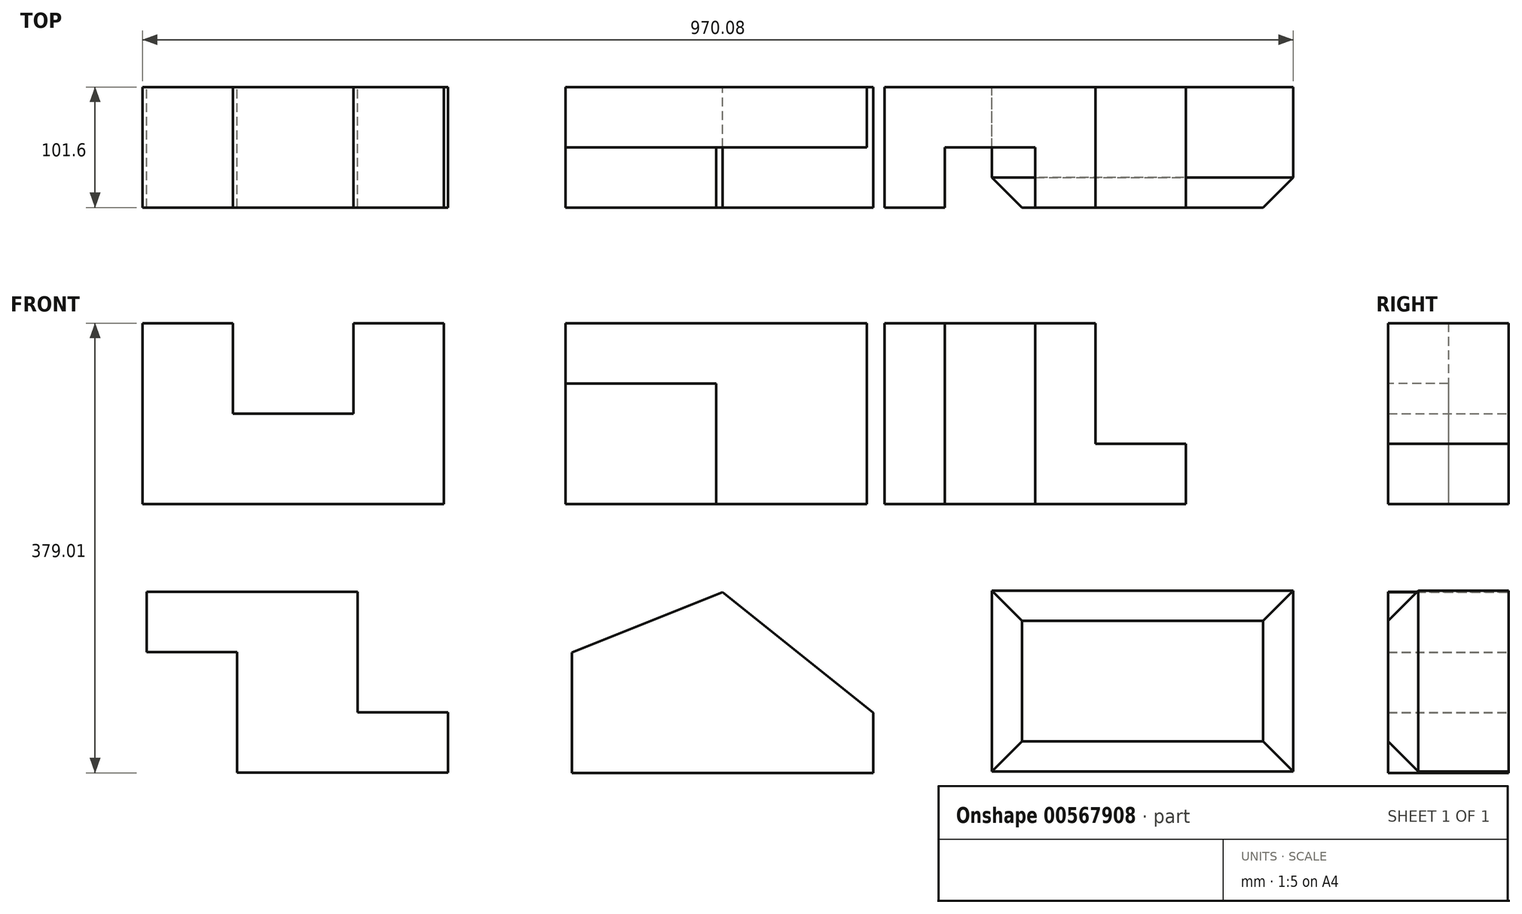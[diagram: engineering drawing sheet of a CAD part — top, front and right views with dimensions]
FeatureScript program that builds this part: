
annotation { "Feature Type Name" : "Feature", "Feature Type Description" : "" }
export const myFeature = defineFeature(function(context is Context, id is Id, definition is map)
    precondition{}
    {
        {
            var Q0;
            Q0=qCreatedBy(makeId("Front.planeOp"),FACE);
            var sketch = newSketch(context, id + "F0", { "sketchPlane" : qUnion([Q0])});
            skLineSegment(sketch, "E0", {"start": v(0, 0) * mm, "end": v(127, 0) * mm});
            skLineSegment(sketch, "E1", {"start": v(0, 0) * mm, "end": v(-127, 0) * mm});
            skLineSegment(sketch, "E2", {"start": v(127, 0) * mm, "end": v(127, 152.4) * mm});
            skLineSegment(sketch, "E3", {"start": v(127, 152.4) * mm, "end": v(50.8, 152.4) * mm});
            skLineSegment(sketch, "E4", {"start": v(50.8, 152.4) * mm, "end": v(50.8, 76.2) * mm});
            skLineSegment(sketch, "E5", {"start": v(50.8, 76.2) * mm, "end": v(-50.8, 76.2) * mm});
            skLineSegment(sketch, "E6", {"start": v(-50.8, 76.2) * mm, "end": v(-50.8, 152.4) * mm});
            skLineSegment(sketch, "E7", {"start": v(-50.8, 152.4) * mm, "end": v(-127, 152.4) * mm});
            skLineSegment(sketch, "E8", {"start": v(-127, 152.4) * mm, "end": v(-127, 0) * mm});
            skSolve(sketch);
        }
        {
            var Q0;
            Q0 = qSketchRegion(id + "F0", true);
            extrude(context, id + "F1", {"entities" : qUnion([Q0]), "depth" : 101.6 * mm, "offsetDistance" : 25.4 * mm});
        }
        {
            var Q0;
            Q0=qCreatedBy(makeId("Top.planeOp"),FACE);
            var sketch = newSketch(context, id + "F2", { "sketchPlane" : qUnion([Q0])});
            skLineSegment(sketch, "E9", {"start": v(229.7, 0) * mm, "end": v(229.7, -101.6) * mm});
            skLineSegment(sketch, "E10", {"start": v(229.7, -101.6) * mm, "end": v(356.7, -101.6) * mm});
            skLineSegment(sketch, "E11", {"start": v(356.7, -101.6) * mm, "end": v(356.7, -50.8) * mm});
            skLineSegment(sketch, "E12", {"start": v(356.7, -50.8) * mm, "end": v(483.7, -50.8) * mm});
            skLineSegment(sketch, "E13", {"start": v(229.7, -101.6) * mm, "end": v(220.96, -101.6) * mm});
            skLineSegment(sketch, "E14", {"start": v(483.7, -50.8) * mm, "end": v(483.7, 0) * mm});
            skLineSegment(sketch, "E15", {"start": v(483.7, 0) * mm, "end": v(229.7, 0) * mm});
            skSolve(sketch);
        }
        {
            var Q0;
            Q0 = qSketchRegion(id + "F2", true);
            extrude(context, id + "F3", {"entities" : qUnion([Q0]), "depth" : 152.4 * mm, "offsetDistance" : 25.4 * mm});
        }
        {
            var Q0;
            Q0=makeQuery(id+"F3.opExtrude","SWEPT_FACE",FACE,{"disambiguationData":[OSD([sQuery(id+"F2.wireOp",EDGE,"E10")])]});
            var sketch = newSketch(context, id + "F4", { "sketchPlane" : qUnion([Q0])});
            skLineSegment(sketch, "E16.bottom", {"start": v(229.7, 152.4) * mm, "end": v(356.7, 152.4) * mm});
            skLineSegment(sketch, "E16.top", {"start": v(229.7, 101.6) * mm, "end": v(356.7, 101.6) * mm});
            skLineSegment(sketch, "E16.left", {"start": v(229.7, 152.4) * mm, "end": v(229.7, 101.6) * mm});
            skLineSegment(sketch, "E16.right", {"start": v(356.7, 152.4) * mm, "end": v(356.7, 101.6) * mm});
            skSolve(sketch);
        }
        {
            var Q0;
            Q0=makeQuery(id+"F4.imprint","IMPRINT",FACE,{"disambiguationData":[TD([[makeQuery(id+"F4.imprint","IMPRINT",EDGE,{"derivedFrom":sQuery(id+"F4.wireOp",EDGE,"E16.bottom")}),-1.0]])]});
            extrude(context, id + "F5", {"entities" : qUnion([Q0]), "operationType" : NewBodyOperationType.REMOVE, "oppositeDirection" : true, "depth" : 50.8 * mm, "offsetDistance" : 25.4 * mm});
        }
        {
            var Q0;
            Q0=qCreatedBy(makeId("Top.planeOp"),FACE);
            var sketch = newSketch(context, id + "F6", { "sketchPlane" : qUnion([Q0])});
            skLineSegment(sketch, "E17", {"start": v(498.64, -101.6) * mm, "end": v(498.64, 0) * mm});
            skLineSegment(sketch, "E18", {"start": v(498.64, -101.6) * mm, "end": v(549.44, -101.6) * mm});
            skLineSegment(sketch, "E19", {"start": v(549.44, -101.6) * mm, "end": v(549.44, -50.8) * mm});
            skLineSegment(sketch, "E20", {"start": v(549.44, -50.8) * mm, "end": v(625.64, -50.8) * mm});
            skLineSegment(sketch, "E21", {"start": v(625.64, -50.8) * mm, "end": v(625.64, -101.6) * mm});
            skLineSegment(sketch, "E22", {"start": v(625.64, -101.6) * mm, "end": v(752.64, -101.6) * mm});
            skLineSegment(sketch, "E23", {"start": v(752.64, -101.6) * mm, "end": v(752.64, 0) * mm});
            skLineSegment(sketch, "E24", {"start": v(752.64, 0) * mm, "end": v(498.64, 0) * mm});
            skSolve(sketch);
        }
        {
            var Q0;
            Q0 = qSketchRegion(id + "F6", true);
            extrude(context, id + "F7", {"entities" : qUnion([Q0]), "depth" : 152.4 * mm, "offsetDistance" : 25.4 * mm});
        }
        {
            var Q0;
            Q0=makeQuery(id+"F7.opExtrude","CAP_FACE",FACE,{"disambiguationData":[OSD([sQuery(id+"F6.wireOp",EDGE,"E17"),sQuery(id+"F6.wireOp",EDGE,"E18"),sQuery(id+"F6.wireOp",EDGE,"E19"),sQuery(id+"F6.wireOp",EDGE,"E20"),sQuery(id+"F6.wireOp",EDGE,"E21"),sQuery(id+"F6.wireOp",EDGE,"E22"),sQuery(id+"F6.wireOp",EDGE,"E23"),sQuery(id+"F6.wireOp",EDGE,"E24")])],"isStart":false});
            var sketch = newSketch(context, id + "F8", { "sketchPlane" : qUnion([Q0])});
            skLineSegment(sketch, "E25.bottom", {"start": v(752.64, -101.6) * mm, "end": v(676.44, -101.6) * mm});
            skLineSegment(sketch, "E25.top", {"start": v(752.64, 0) * mm, "end": v(676.44, 0) * mm});
            skLineSegment(sketch, "E25.left", {"start": v(752.64, -101.6) * mm, "end": v(752.64, 0) * mm});
            skLineSegment(sketch, "E25.right", {"start": v(676.44, -101.6) * mm, "end": v(676.44, 0) * mm});
            skSolve(sketch);
        }
        {
            var Q0;
            Q0=makeQuery(id+"F8.imprint","IMPRINT",FACE,{"disambiguationData":[TD([[makeQuery(id+"F8.imprint","IMPRINT",EDGE,{"derivedFrom":sQuery(id+"F8.wireOp",EDGE,"E25.bottom")}),1.0]])]});
            extrude(context, id + "F9", {"entities" : qUnion([Q0]), "operationType" : NewBodyOperationType.REMOVE, "oppositeDirection" : true, "depth" : 101.6 * mm, "offsetDistance" : 25.4 * mm});
        }
        {
            var Q0;
            Q0=qCreatedBy(makeId("Front.planeOp"),FACE);
            var sketch = newSketch(context, id + "F10", { "sketchPlane" : qUnion([Q0])});
            skLineSegment(sketch, "E26", {"start": v(-123.4, 0) * mm, "end": v(-123.4, -74.16) * mm});
            skLineSegment(sketch, "E27", {"start": v(-123.4, -74.16) * mm, "end": v(-123.4, -124.96) * mm});
            skLineSegment(sketch, "E28", {"start": v(-123.4, -74.16) * mm, "end": v(54.4, -74.16) * mm});
            skLineSegment(sketch, "E29", {"start": v(54.4, -74.16) * mm, "end": v(54.4, -175.76) * mm});
            skLineSegment(sketch, "E30", {"start": v(54.4, -175.76) * mm, "end": v(130.6, -175.76) * mm});
            skLineSegment(sketch, "E31", {"start": v(130.6, -175.76) * mm, "end": v(130.6, -226.56) * mm});
            skLineSegment(sketch, "E32", {"start": v(130.6, -226.56) * mm, "end": v(-47.2, -226.56) * mm});
            skLineSegment(sketch, "E33", {"start": v(-47.2, -226.56) * mm, "end": v(-47.2, -124.96) * mm});
            skLineSegment(sketch, "E34", {"start": v(-47.2, -124.96) * mm, "end": v(-123.4, -124.96) * mm});
            skSolve(sketch);
        }
        {
            var Q0;
            Q0 = qSketchRegion(id + "F10", true);
            extrude(context, id + "F11", {"entities" : qUnion([Q0]), "depth" : 101.6 * mm, "offsetDistance" : 25.4 * mm});
        }
        {
            var Q0;
            Q0=qCreatedBy(makeId("Front.planeOp"),FACE);
            var sketch = newSketch(context, id + "F12", { "sketchPlane" : qUnion([Q0])});
            skLineSegment(sketch, "E35", {"start": v(234.94, -226.61) * mm, "end": v(488.94, -226.61) * mm});
            skLineSegment(sketch, "E36", {"start": v(488.94, -226.61) * mm, "end": v(488.94, -175.81) * mm});
            skLineSegment(sketch, "E37", {"start": v(234.94, -226.61) * mm, "end": v(234.94, -125.01) * mm});
            skLineSegment(sketch, "E38", {"start": v(234.94, -226.61) * mm, "end": v(361.94, -226.61) * mm});
            skLineSegment(sketch, "E39", {"start": v(361.94, -74.21) * mm, "end": v(234.94, -125.01) * mm});
            skLineSegment(sketch, "E40", {"start": v(361.94, -74.21) * mm, "end": v(488.94, -175.81) * mm});
            skSolve(sketch);
        }
        {
            var Q0;
            Q0 = qSketchRegion(id + "F12", true);
            extrude(context, id + "F13", {"entities" : qUnion([Q0]), "depth" : 101.6 * mm, "offsetDistance" : 25.4 * mm});
        }
        {
            var Q0;
            Q0=qCreatedBy(makeId("Front.planeOp"),FACE);
            var sketch = newSketch(context, id + "F14", { "sketchPlane" : qUnion([Q0])});
            skLineSegment(sketch, "E41", {"start": v(589.08, -225.44) * mm, "end": v(589.08, -73.04) * mm});
            skLineSegment(sketch, "E42", {"start": v(589.08, -73.04) * mm, "end": v(843.08, -73.04) * mm});
            skLineSegment(sketch, "E43", {"start": v(843.08, -73.04) * mm, "end": v(843.08, -225.44) * mm});
            skLineSegment(sketch, "E44", {"start": v(843.08, -225.44) * mm, "end": v(589.08, -225.44) * mm});
            skSolve(sketch);
        }
        {
            var Q0;
            Q0 = qSketchRegion(id + "F14", true);
            extrude(context, id + "F15", {"entities" : qUnion([Q0]), "depth" : 101.6 * mm, "offsetDistance" : 25.4 * mm});
        }
        {
            var Q0;
            Q0=makeQuery(id+"F15.opExtrude","CAP_EDGE",EDGE,{"disambiguationData":[OSD([sQuery(id+"F14.wireOp",EDGE,"E42")])],"isStart":false});
            chamfer(context, id + "F16", {"entities" : qUnion([Q0]), "width" : 25.4 * mm, "tangentPropagation" : true});
        }
        {
            var Q0;
            Q0=makeQuery(id+"F15.opExtrude","CAP_EDGE",EDGE,{"disambiguationData":[OSD([sQuery(id+"F14.wireOp",EDGE,"E43")])],"isStart":false});
            var Q1;
            Q1=makeQuery(id+"F15.opExtrude","CAP_EDGE",EDGE,{"disambiguationData":[OSD([sQuery(id+"F14.wireOp",EDGE,"E44")])],"isStart":false});
            chamfer(context, id + "F17", {"entities" : qUnion([Q0, Q1]), "width" : 25.4 * mm, "tangentPropagation" : true});
        }
        {
            var Q0;
            Q0=makeQuery(id+"F15.opExtrude","CAP_EDGE",EDGE,{"disambiguationData":[OSD([sQuery(id+"F14.wireOp",EDGE,"E41")])],"isStart":false});
            chamfer(context, id + "F18", {"entities" : qUnion([Q0]), "width" : 25.4 * mm, "tangentPropagation" : true});
        }
    });
